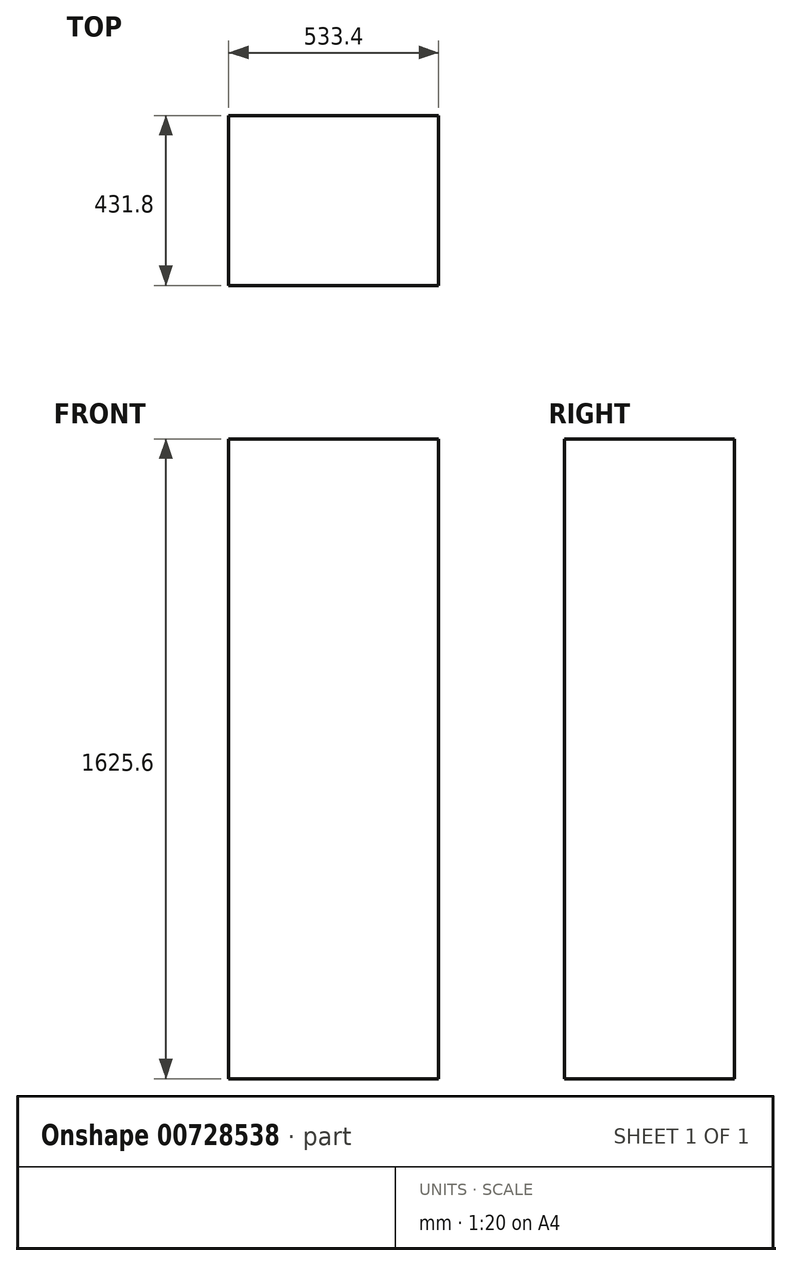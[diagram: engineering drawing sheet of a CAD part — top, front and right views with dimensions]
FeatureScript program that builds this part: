
annotation { "Feature Type Name" : "Feature", "Feature Type Description" : "" }
export const myFeature = defineFeature(function(context is Context, id is Id, definition is map)
    precondition{}
    {
        {
            var Q0;
            Q0=qCreatedBy(makeId("Top.planeOp"),FACE);
            var sketch = newSketch(context, id + "F0", { "sketchPlane" : qUnion([Q0])});
            skLineSegment(sketch, "E0.bottom", {"start": v(266.7, 215.9) * mm, "end": v(-266.7, 215.9) * mm});
            skLineSegment(sketch, "E0.top", {"start": v(266.7, -215.9) * mm, "end": v(-266.7, -215.9) * mm});
            skLineSegment(sketch, "E0.left", {"start": v(266.7, 215.9) * mm, "end": v(266.7, -215.9) * mm});
            skLineSegment(sketch, "E0.right", {"start": v(-266.7, 215.9) * mm, "end": v(-266.7, -215.9) * mm});
            skPoint(sketch, "E0.middle", {"position": v(0, 0) * mm});
            skSolve(sketch);
        }
        {
            var Q0;
            Q0 = qSketchRegion(id + "F0", true);
            extrude(context, id + "F1", {"entities" : qUnion([Q0]), "depth" : 1625.6 * mm, "offsetDistance" : 25.4 * mm});
        }
    });
